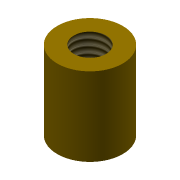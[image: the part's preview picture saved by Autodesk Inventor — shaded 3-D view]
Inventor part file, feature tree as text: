
AUTODESK INVENTOR PART (.ipt)
format: ipt  version: 2022 (Build 260153000, 153)  size: 86,528 bytes
history: native  units: mm
features: sketch x2, extrude x1, hole x1
ambient origin geometry x8: Origin, YZ Plane, XZ Plane, XY Plane, X Axis, Y Axis, Z Axis, Center Point
bodies: Solid1 (feature_tree)
feature tree (4):
  extrude  "Extrusion1"  Depth=6.0mm TaperAngle=0.0deg
  hole  "Hole1"  [1 undecoded]
  sketch  "Sketch1"  dims[d0=5.0mm d1=6.0mm d2=0.0mm]
  sketch  "Sketch2"  dims[d3=2.459mm d4=10.0mm d5=4.0mm d6=2.0mm d7=90.0deg d8=8.0mm d9=20.594885mm]
note: 1 required parameter value undecoded (feature->parameter linkage not recoverable at this tier; creation-order binding heuristic only, values carry confidence <= 0.55)
